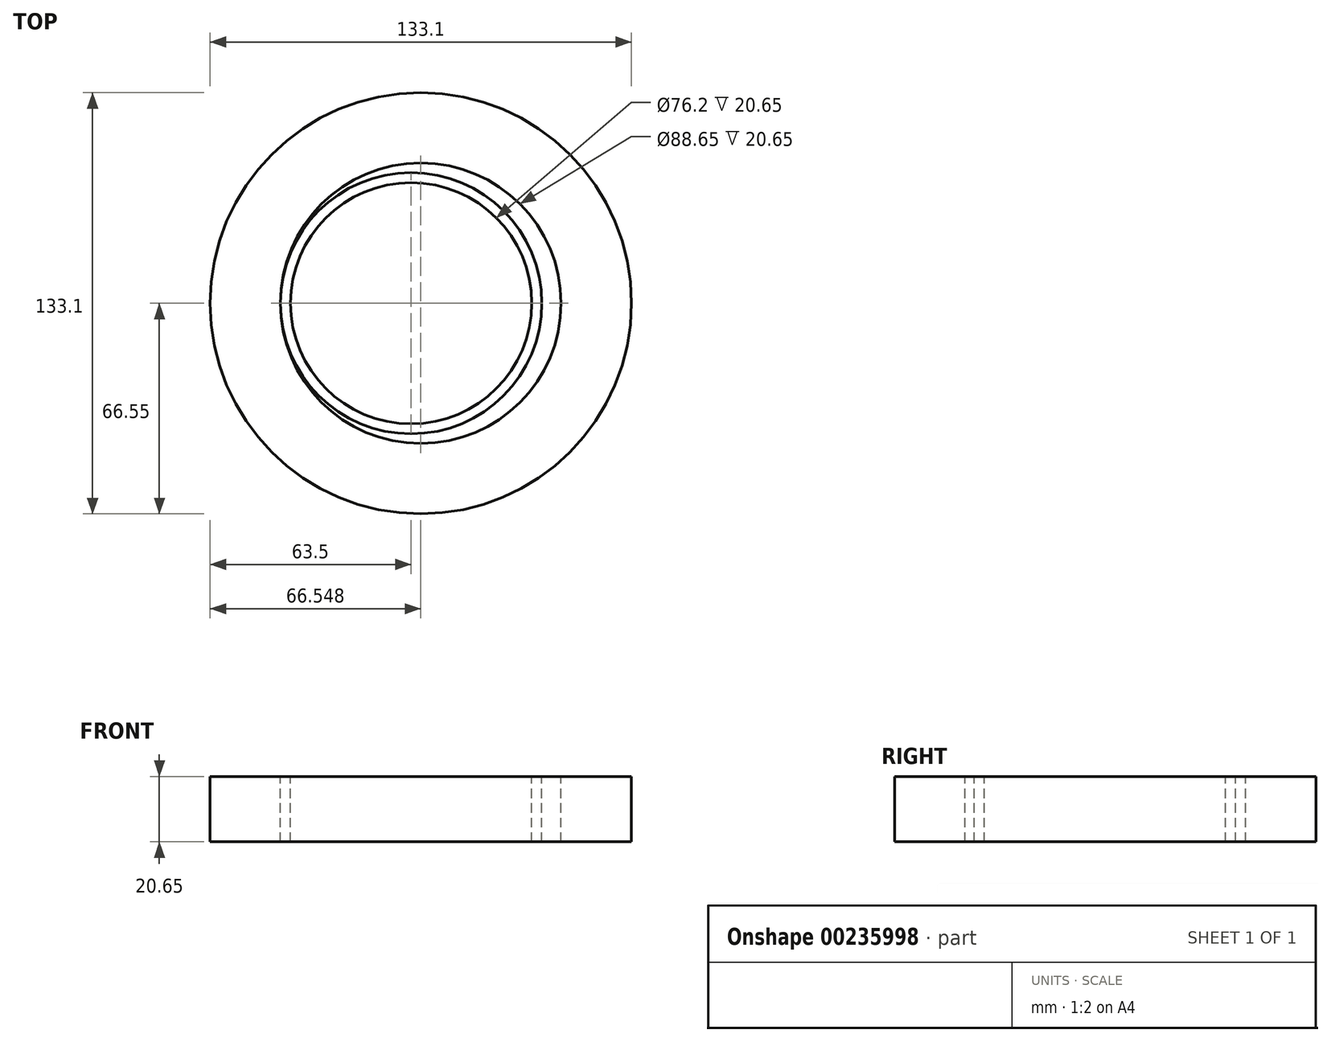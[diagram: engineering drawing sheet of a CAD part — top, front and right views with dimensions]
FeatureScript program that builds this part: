
annotation { "Feature Type Name" : "Feature", "Feature Type Description" : "" }
export const myFeature = defineFeature(function(context is Context, id is Id, definition is map)
    precondition{}
    {
        {
            var Q0;
            Q0=qCreatedBy(makeId("Front.planeOp"),FACE);
            var sketch = newSketch(context, id + "F0", { "sketchPlane" : qUnion([Q0])});
            skLineSegment(sketch, "E0.bottom", {"start": v(0, 0) * mm, "end": v(-3.17, 0) * mm});
            skLineSegment(sketch, "E0.top", {"start": v(0, 20.65) * mm, "end": v(-3.18, 20.65) * mm});
            skLineSegment(sketch, "E0.left", {"start": v(0, 0) * mm, "end": v(0, 20.65) * mm});
            skLineSegment(sketch, "E0.right", {"start": v(-3.17, 0) * mm, "end": v(-3.18, 20.65) * mm});
            skLineSegment(sketch, "E1", {"start": v(38.1, 22.48) * mm, "end": v(38.1, -15.25) * mm, "construction": true});
            skSolve(sketch);
        }
        {
            var Q0;
            Q0=qCreatedBy(makeId("Front.planeOp"),FACE);
            var sketch = newSketch(context, id + "F1", { "sketchPlane" : qUnion([Q0])});
            skLineSegment(sketch, "E2.0", {"start": v(-3.17, 0) * mm, "end": v(-3.18, 20.65) * mm});
            skLineSegment(sketch, "E3.bottom", {"start": v(-3.17, 0) * mm, "end": v(-25.4, 0) * mm});
            skLineSegment(sketch, "E3.top", {"start": v(-3.18, 20.65) * mm, "end": v(-25.4, 20.65) * mm});
            skLineSegment(sketch, "E3.left", {"start": v(-3.17, 0) * mm, "end": v(-3.17, 20.65) * mm});
            skLineSegment(sketch, "E3.right", {"start": v(-25.4, 0) * mm, "end": v(-25.4, 20.65) * mm});
            skLineSegment(sketch, "E4", {"start": v(41.15, 30.65) * mm, "end": v(41.15, -11.79) * mm, "construction": true});
            skSolve(sketch);
        }
        {
            var Q0;
            Q0=makeQuery(id+"F0.imprint","IMPRINT",FACE,{"disambiguationData":[TD([[makeQuery(id+"F0.imprint","IMPRINT",EDGE,{"derivedFrom":sQuery(id+"F0.wireOp",EDGE,"E0.bottom")}),-1.0]])]});
            var Q1;
            Q1=sQuery(id+"F0.wireOp",EDGE,"E1");
            revolve(context, id + "F2", {"entities" : qUnion([Q0]), "axis" : qUnion([Q1]), "revolveType" : RevolveType.FULL});
        }
        {
            var Q0;
            Q0=makeQuery(id+"F1.imprint","IMPRINT",FACE,{"disambiguationData":[TD([[makeQuery(id+"F1.imprint","IMPRINT",EDGE,{"derivedFrom":sQuery(id+"F1.wireOp",EDGE,"E3.bottom")}),-1.0]])]});
            var Q1;
            Q1=sQuery(id+"F1.wireOp",EDGE,"E4");
            revolve(context, id + "F3", {"operationType" : NewBodyOperationType.ADD, "entities" : qUnion([Q0]), "axis" : qUnion([Q1]), "revolveType" : RevolveType.FULL});
        }
    });
